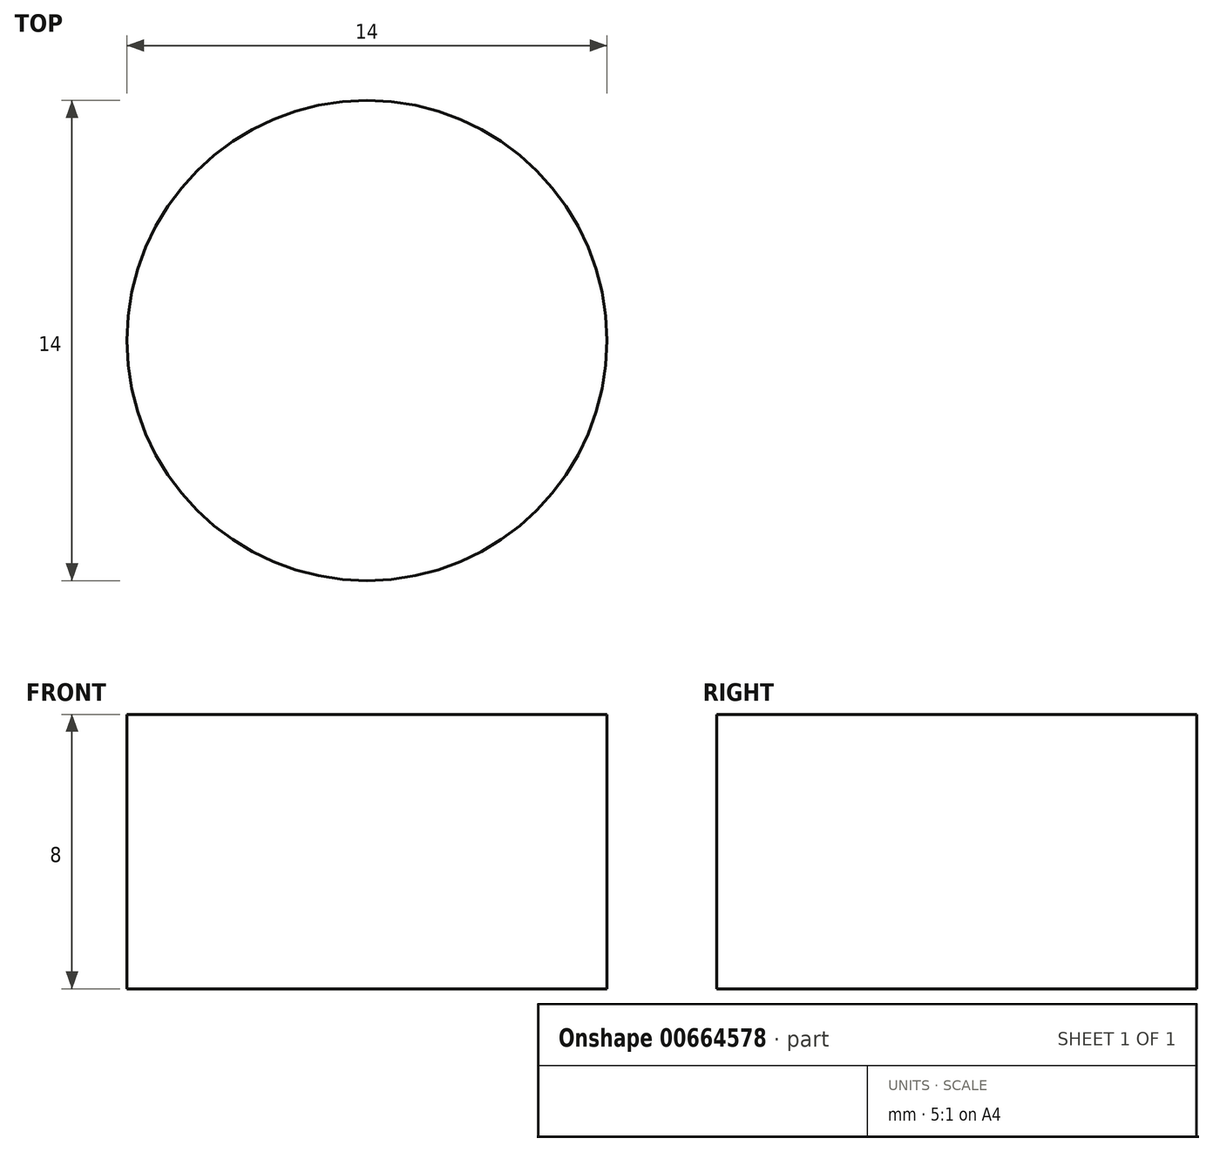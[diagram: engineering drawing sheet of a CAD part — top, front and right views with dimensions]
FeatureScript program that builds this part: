
annotation { "Feature Type Name" : "Feature", "Feature Type Description" : "" }
export const myFeature = defineFeature(function(context is Context, id is Id, definition is map)
    precondition{}
    {
        {
            var Q0;
            Q0=qCreatedBy(makeId("Top.planeOp"),FACE);
            var sketch = newSketch(context, id + "F0", { "sketchPlane" : qUnion([Q0])});
            skCircle(sketch, "E0", {"center": v(0, 0) * mm, "radius": 7 * mm});
            skSolve(sketch);
        }
        {
            var Q0;
            Q0 = qSketchRegion(id + "F0", true);
            extrude(context, id + "F1", {"entities" : qUnion([Q0]), "depth" : 8 * mm, "offsetDistance" : 25 * mm});
        }
    });
